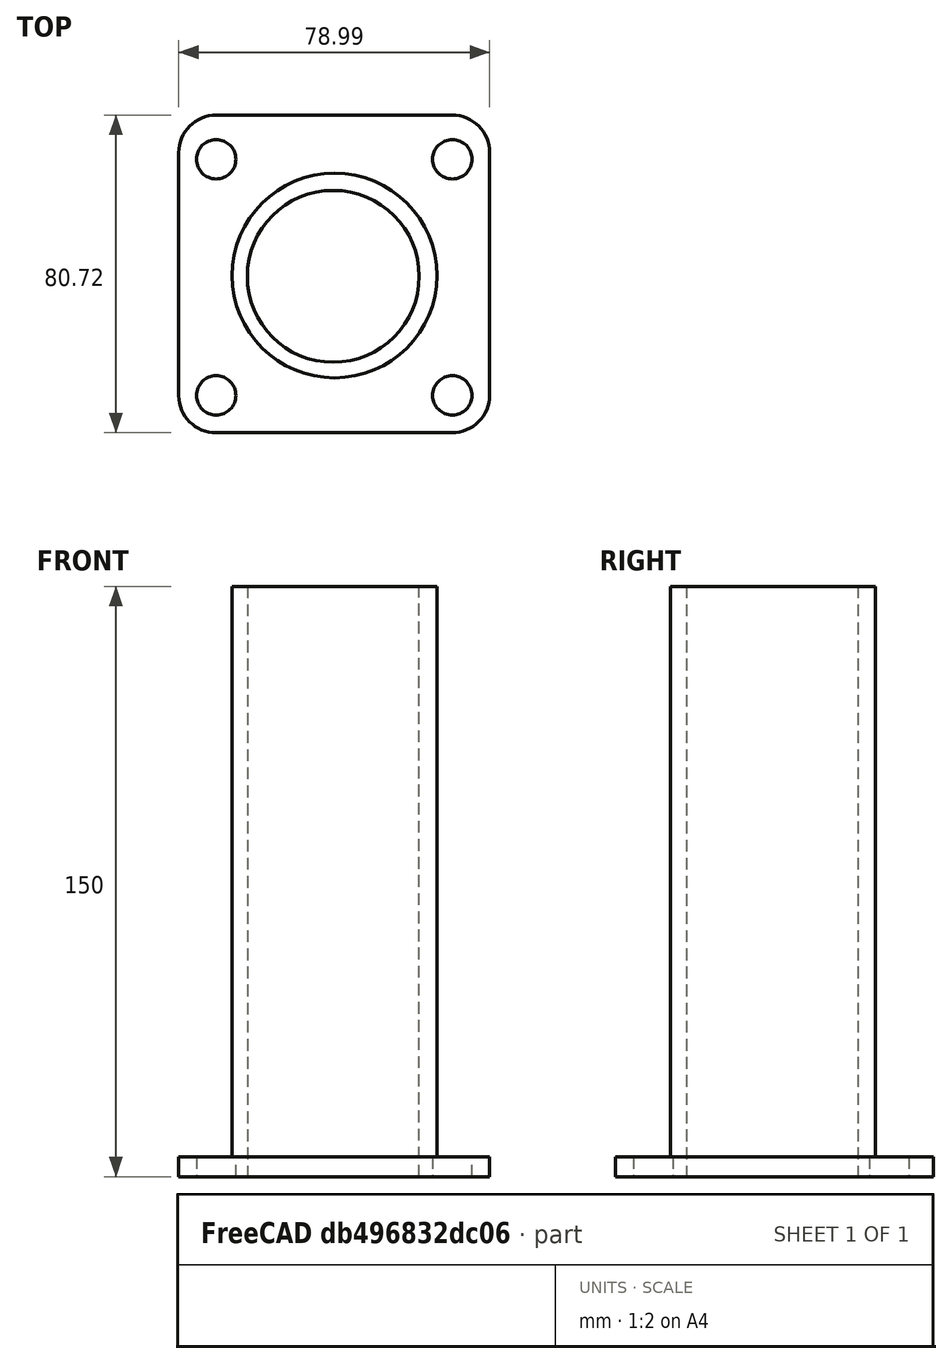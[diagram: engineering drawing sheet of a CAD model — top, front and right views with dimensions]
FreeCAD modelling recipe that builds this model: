
FCSTD DOCUMENT  (FreeCAD 0.18R16131 (Git))
Label: Cylinder_test1
License: All rights reserved
LicenseURL: http://en.wikipedia.org/wiki/All_rights_reserved
objects: Sketcher::SketchObject×3, PartDesign::Pad×2, PartDesign::Pocket×1, PartDesign::Body×1
note: 10 computed .brp shape members not serialized (recipe doc carries the construction recipe); baked Part::Feature solids carry a one-line shape summary decoded from their .brp

FEATURE [Sketcher::SketchObject] Sketch
  MapMode = 5
  Support = -> [XY_Plane]
  sketch-geometry (12):
    g0: LineSegment StartX=-29.7651 StartY=-39.7508 StartZ=0 EndX=30.1817 EndY=-39.7508 EndZ=0
    g1: LineSegment StartX=39.7595 StartY=-30.173 StartZ=0 EndX=39.7595 EndY=31.4703 EndZ=0
    g2: LineSegment StartX=30.2634 StartY=40.9665 StartZ=0 EndX=-29.735 EndY=40.9665 EndZ=0
    g3: LineSegment StartX=-39.2312 StartY=31.4703 StartZ=0 EndX=-39.2312 EndY=-30.2847 EndZ=0
    g4: Circle CenterX=-29.735 CenterY=29.7438 CenterZ=0 NormalX=0 NormalY=0 NormalZ=1 AngleXU=0 Radius=5
    g5: Circle CenterX=30.2634 CenterY=29.7438 CenterZ=0 NormalX=0 NormalY=0 NormalZ=1 AngleXU=0 Radius=5
    g6: Circle CenterX=-29.735 CenterY=-30.2546 CenterZ=0 NormalX=0 NormalY=0 NormalZ=1 AngleXU=0 Radius=5
    g7: Circle CenterX=30.2634 CenterY=-30.2546 CenterZ=0 NormalX=0 NormalY=0 NormalZ=1 AngleXU=0 Radius=5
    g8: ArcOfCircle CenterX=-29.735 CenterY=31.4703 CenterZ=0 NormalX=0 NormalY=0 NormalZ=1 AngleXU=0 Radius=9.49615 StartAngle=1.5708 EndAngle=3.14159
    g9: ArcOfCircle CenterX=30.2634 CenterY=31.4703 CenterZ=0 NormalX=0 NormalY=0 NormalZ=1 AngleXU=0 Radius=9.49617 StartAngle=0 EndAngle=1.5708
    g10: ArcOfCircle CenterX=30.1817 CenterY=-30.173 CenterZ=0 NormalX=0 NormalY=0 NormalZ=1 AngleXU=0 Radius=9.57781 StartAngle=4.71239 EndAngle=6.28319
    g11: ArcOfCircle CenterX=-29.7651 CenterY=-30.2847 CenterZ=0 NormalX=0 NormalY=0 NormalZ=1 AngleXU=0 Radius=9.4661 StartAngle=3.14159 EndAngle=4.71239
  constraints (16):
    c: Horizontal(g0)
    c: Horizontal(g2)
    c: Vertical(g1)
    c: Vertical(g3)
    c: Radius(g4) = 5
    c: Radius(g5) = 5
    c: Radius(g6) = 5
    c: Radius(g7) = 5
    c: Tangent(g2,g8) = -1.5708
    c: Tangent(g3,g8) = -1.5708
    c: Tangent(g2,g9) = -1.5708
    c: Tangent(g1,g9) = -1.5708
    c: Tangent(g1,g10) = -1.5708
    c: Tangent(g0,g10) = -1.5708
    c: Tangent(g0,g11) = -1.5708
    c: Tangent(g3,g11) = -1.5708
FEATURE [PartDesign::Pad] Pad
  Length = 5
  Length2 = 100
  Profile = -> Sketch
  Type = 0
FEATURE [Sketcher::SketchObject] Sketch001
  MapMode = 5
  Placement = pos=(0,0,0) rot=(1,0,0;3.14159rad)
  Support = -> [Pad]
  sketch-geometry (1):
    g0: Circle CenterX=0 CenterY=0 CenterZ=0 NormalX=0 NormalY=0 NormalZ=1 AngleXU=0 Radius=21.8296
FEATURE [Sketcher::SketchObject] Sketch002
  MapMode = 5
  Support = -> [XY_Plane]
  sketch-geometry (1):
    g0: Circle CenterX=0.332326 CenterY=0.20453 CenterZ=0 NormalX=0 NormalY=0 NormalZ=1 AngleXU=0 Radius=26
  constraints (1):
    c: Radius(g0) = 26
FEATURE [PartDesign::Pad] Pad001
  BaseFeature = -> Pad
  Length = 150
  Length2 = 100
  Profile = -> Sketch002
  Type = 0
FEATURE [PartDesign::Pocket] Pocket
  BaseFeature = -> Pad001
  Length = 150
  Length2 = 100
  Profile = -> Sketch001
  Type = 0
FEATURE [PartDesign::Body] Body
  Group = -> [Sketch,Pad,Sketch001,Sketch002,Pad001,Pocket]
  Origin = -> Origin
  Tip = -> Pocket
